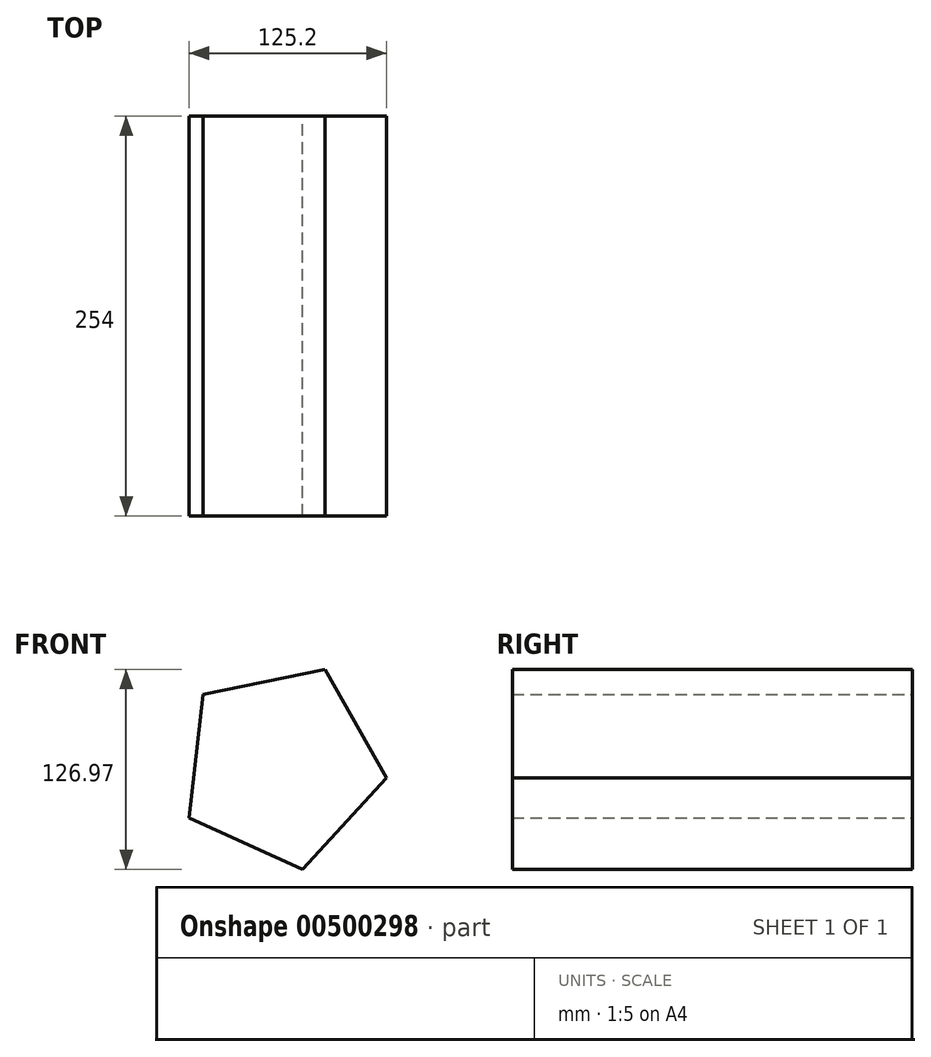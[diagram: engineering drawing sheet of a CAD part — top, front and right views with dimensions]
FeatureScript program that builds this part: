
annotation { "Feature Type Name" : "Feature", "Feature Type Description" : "" }
export const myFeature = defineFeature(function(context is Context, id is Id, definition is map)
    precondition{}
    {
        {
            var Q0;
            Q0=qCreatedBy(makeId("Front.planeOp"),FACE);
            var sketch = newSketch(context, id + "F0", { "sketchPlane" : qUnion([Q0])});
            skCircle(sketch, "E0.cCircle", {"center": v(0, 0) * mm, "radius": 67.18 * mm, "construction": true});
            skLineSegment(sketch, "E0.0", {"start": v(-49.56, 45.36) * mm, "end": v(27.82, 61.15) * mm});
            skLineSegment(sketch, "E0.1", {"start": v(27.82, 61.15) * mm, "end": v(66.75, -7.56) * mm});
            skLineSegment(sketch, "E0.2", {"start": v(66.75, -7.56) * mm, "end": v(13.44, -65.82) * mm});
            skLineSegment(sketch, "E0.3", {"start": v(13.44, -65.82) * mm, "end": v(-58.45, -33.12) * mm});
            skLineSegment(sketch, "E0.4", {"start": v(-58.45, -33.12) * mm, "end": v(-49.56, 45.36) * mm});
            skSolve(sketch);
        }
        {
            var Q0;
            Q0=makeQuery(id+"F0.imprint","IMPRINT",FACE,{"disambiguationData":[TD([[makeQuery(id+"F0.imprint","IMPRINT",EDGE,{"derivedFrom":sQuery(id+"F0.wireOp",EDGE,"E0.0")}),-1.0]])]});
            extrude(context, id + "F1", {"entities" : qUnion([Q0]), "endBound" : BoundingType.SYMMETRIC, "depth" : 254 * mm});
        }
    });
